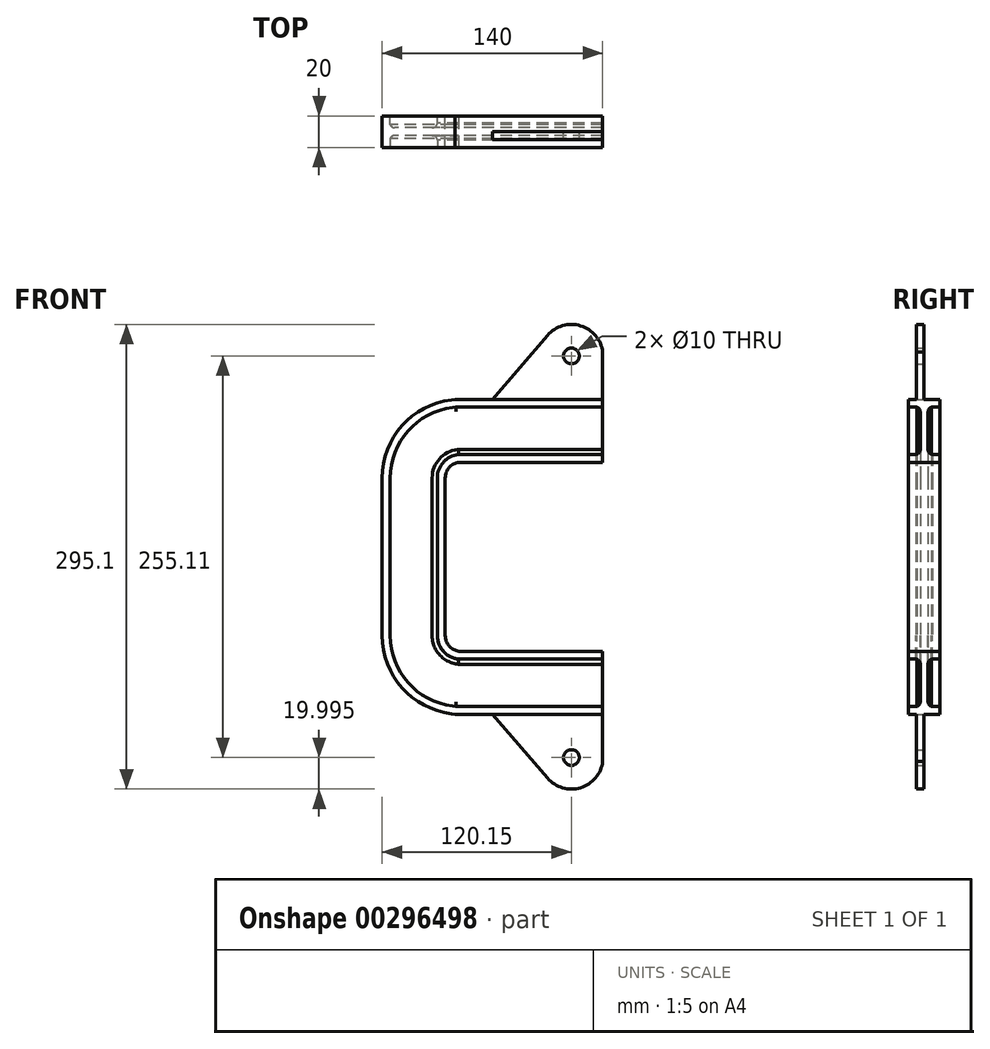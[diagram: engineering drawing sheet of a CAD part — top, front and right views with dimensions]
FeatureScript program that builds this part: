
annotation { "Feature Type Name" : "Feature", "Feature Type Description" : "" }
export const myFeature = defineFeature(function(context is Context, id is Id, definition is map)
    precondition{}
    {
        {
            var Q0;
            Q0=qCreatedBy(makeId("Front.planeOp"),FACE);
            var sketch = newSketch(context, id + "F0", { "sketchPlane" : qUnion([Q0])});
            skLineSegment(sketch, "E0", {"start": v(0, 60) * mm, "end": v(-91.21, 60) * mm});
            skLineSegment(sketch, "E1", {"start": v(-100, 50.07) * mm, "end": v(-100, 0) * mm});
            skArc(sketch, "E2", {"start": v(-91.21, 60) * mm, "mid": v(-97.49, 56.7) * mm, "end": v(-100, 50.07) * mm});
            skSolve(sketch);
        }
        {
            var Q0;
            Q0=qCreatedBy(makeId("Right.planeOp"),FACE);
            var sketch = newSketch(context, id + "F1", { "sketchPlane" : qUnion([Q0])});
            skArc(sketch, "E3", {"start": v(2.5, 68.29) * mm, "mid": v(3.23, 66.02) * mm, "end": v(5.38, 65) * mm});
            skLineSegment(sketch, "E4", {"start": v(2.5, 68.29) * mm, "end": v(2.5, 92.17) * mm});
            skArc(sketch, "E5", {"start": v(4.5, 95) * mm, "mid": v(3.05, 93.9) * mm, "end": v(2.5, 92.17) * mm});
            skLineSegment(sketch, "E6", {"start": v(4.5, 95) * mm, "end": v(10, 95) * mm});
            skLineSegment(sketch, "E7", {"start": v(10, 95) * mm, "end": v(10, 100) * mm});
            skLineSegment(sketch, "E8", {"start": v(10, 100) * mm, "end": v(0, 100) * mm});
            skArc(sketch, "E9.MirrorCS", {"start": v(-4.5, 95) * mm, "mid": v(-3.05, 93.9) * mm, "end": v(-2.5, 92.17) * mm});
            skLineSegment(sketch, "E10.MirrorCS", {"start": v(-10, 95) * mm, "end": v(-10, 100) * mm});
            skLineSegment(sketch, "E11.MirrorCS", {"start": v(-4.5, 95) * mm, "end": v(-10, 95) * mm});
            skArc(sketch, "E12.MirrorCS", {"start": v(-2.5, 68.29) * mm, "mid": v(-3.23, 66.02) * mm, "end": v(-5.38, 65) * mm});
            skLineSegment(sketch, "E13.MirrorCS", {"start": v(-2.5, 68.29) * mm, "end": v(-2.5, 92.17) * mm});
            skLineSegment(sketch, "E14.MirrorCS", {"start": v(-10, 100) * mm, "end": v(0, 100) * mm});
            skLineSegment(sketch, "E15", {"start": v(5.38, 65) * mm, "end": v(10, 65) * mm});
            skLineSegment(sketch, "E16", {"start": v(10, 65) * mm, "end": v(10, 60) * mm});
            skLineSegment(sketch, "E17", {"start": v(10, 60) * mm, "end": v(0, 60) * mm});
            skLineSegment(sketch, "E18.MirrorCS", {"start": v(-10, 60) * mm, "end": v(0, 60) * mm});
            skLineSegment(sketch, "E19.MirrorCS", {"start": v(-5.38, 65) * mm, "end": v(-10, 65) * mm});
            skLineSegment(sketch, "E20.MirrorCS", {"start": v(-10, 65) * mm, "end": v(-10, 60) * mm});
            skSolve(sketch);
        }
        {
            var Q0;
            Q0=makeQuery(id+"F1.imprint","IMPRINT",FACE,{"disambiguationData":[TD([[makeQuery(id+"F1.imprint","IMPRINT",EDGE,{"derivedFrom":sQuery(id+"F1.wireOp",EDGE,"E3")}),-1.0]])]});
            var Q1;
            Q1=sQuery(id+"F0.wireOp",EDGE,"E0");
            var Q2;
            Q2=sQuery(id+"F0.wireOp",EDGE,"E2");
            var Q3;
            Q3=sQuery(id+"F0.wireOp",EDGE,"E1");
            sweep(context, id + "F2", {"profiles" : qUnion([Q0]), "path" : qUnion([Q1, Q2, Q3])});
        }
        {
            var Q0;
            Q0=makeQuery(id+"F2.opSweep","SWEPT_BODY",BODY,{"disambiguationData":[OSD([sQuery(id+"F0.wireOp",EDGE,"E1"),sQuery(id+"F1.wireOp",EDGE,"E3"),sQuery(id+"F1.wireOp",EDGE,"E4"),sQuery(id+"F1.wireOp",EDGE,"E5"),sQuery(id+"F1.wireOp",EDGE,"E6"),sQuery(id+"F1.wireOp",EDGE,"E7"),sQuery(id+"F1.wireOp",EDGE,"E8"),sQuery(id+"F1.wireOp",EDGE,"E9.MirrorCS"),sQuery(id+"F1.wireOp",EDGE,"E10.MirrorCS"),sQuery(id+"F1.wireOp",EDGE,"E11.MirrorCS"),sQuery(id+"F1.wireOp",EDGE,"E12.MirrorCS"),sQuery(id+"F1.wireOp",EDGE,"E13.MirrorCS"),sQuery(id+"F1.wireOp",EDGE,"E14.MirrorCS"),sQuery(id+"F1.wireOp",EDGE,"E15"),sQuery(id+"F1.wireOp",EDGE,"E16"),sQuery(id+"F1.wireOp",EDGE,"E17"),sQuery(id+"F1.wireOp",EDGE,"E18.MirrorCS"),sQuery(id+"F1.wireOp",EDGE,"E19.MirrorCS"),sQuery(id+"F1.wireOp",EDGE,"E20.MirrorCS")])]});
            var Q1;
            Q1=qCreatedBy(makeId("Top.planeOp"),FACE);
            mirror(context, id + "F3", {"operationType" : NewBodyOperationType.ADD, "entities" : qUnion([Q0]), "mirrorPlane" : qUnion([Q1])});
        }
        {
            var Q0;
            Q0=qCreatedBy(makeId("Front.planeOp"),FACE);
            var sketch = newSketch(context, id + "F4", { "sketchPlane" : qUnion([Q0])});
            skLineSegment(sketch, "E21", {"start": v(0, 100) * mm, "end": v(-70, 100) * mm});
            skLineSegment(sketch, "E22", {"start": v(-70, 100) * mm, "end": v(-35, 140.61) * mm});
            skPoint(sketch, "E22.endSnap0", {"position": v(-35, 100) * mm});
            skLineSegment(sketch, "E23", {"start": v(0, 100) * mm, "end": v(0, 130) * mm});
            skArc(sketch, "E24", {"start": v(0, 130) * mm, "mid": v(-14.05, 146.7) * mm, "end": v(-35, 140.61) * mm});
            skCircle(sketch, "E25", {"center": v(-19.85, 127.55) * mm, "radius": 5 * mm});
            skCircle(sketch, "E26.MirrorC", {"center": v(-19.85, -127.55) * mm, "radius": 5 * mm});
            skPoint(sketch, "E27.MirrorP", {"position": v(-35, -100) * mm});
            skArc(sketch, "E28.MirrorCS", {"start": v(0, -130) * mm, "mid": v(-14.05, -146.7) * mm, "end": v(-35, -140.61) * mm});
            skLineSegment(sketch, "E29.MirrorCS", {"start": v(-70, -100) * mm, "end": v(-35, -140.61) * mm});
            skLineSegment(sketch, "E30.MirrorCS", {"start": v(0, -100) * mm, "end": v(-70, -100) * mm});
            skLineSegment(sketch, "E31.MirrorCS", {"start": v(0, -100) * mm, "end": v(0, -130) * mm});
            skSolve(sketch);
        }
        {
            var Q0;
            Q0 = qSketchRegion(id + "F4", true);
            extrude(context, id + "F5", {"entities" : qUnion([Q0]), "operationType" : NewBodyOperationType.ADD, "depth" : 5 * mm});
        }
    });
